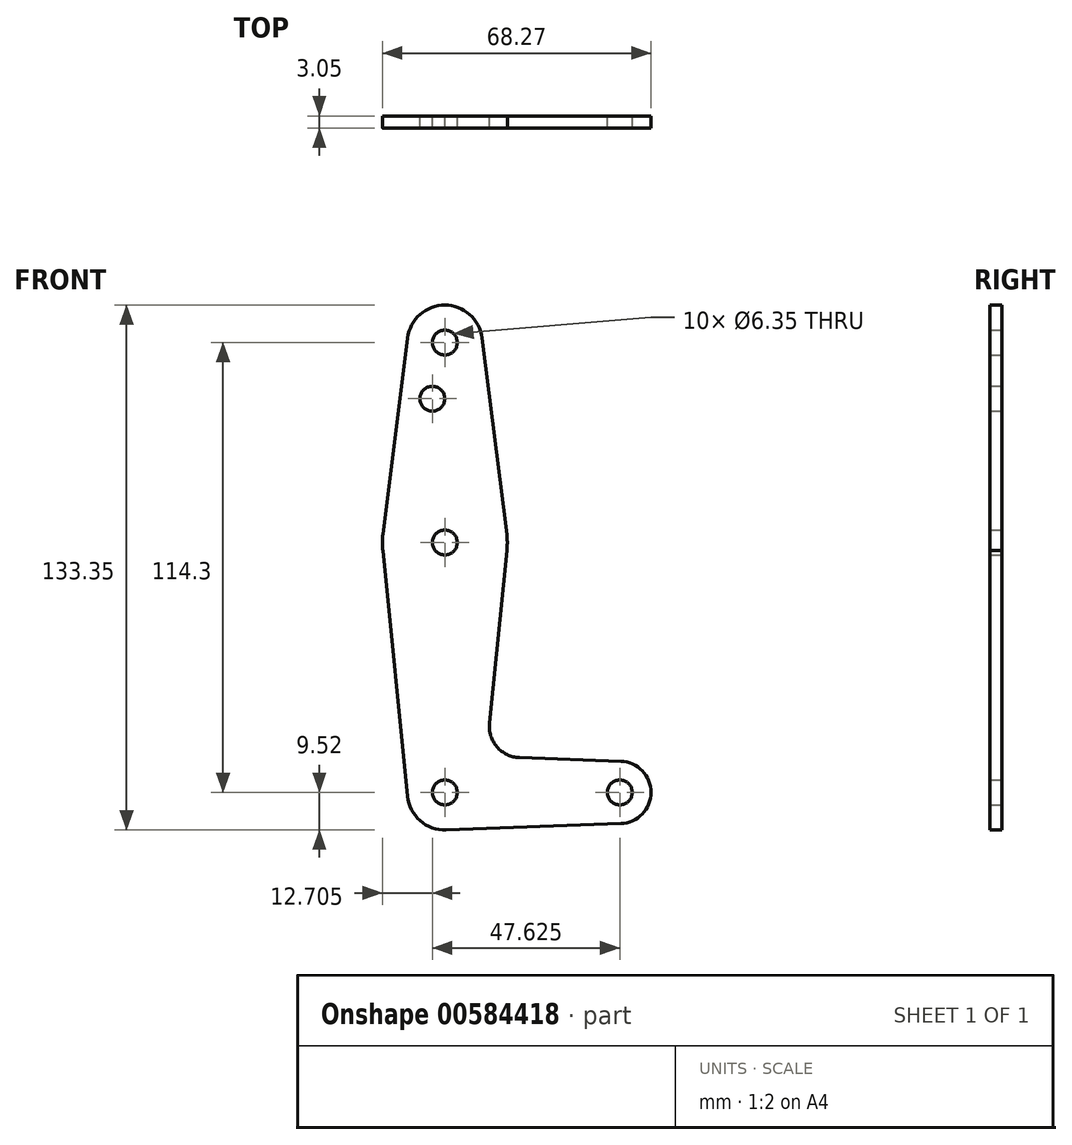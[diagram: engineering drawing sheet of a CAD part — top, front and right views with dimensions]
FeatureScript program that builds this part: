
annotation { "Feature Type Name" : "Feature", "Feature Type Description" : "" }
export const myFeature = defineFeature(function(context is Context, id is Id, definition is map)
    precondition{}
    {
        {
            var Q0;
            Q0=qCreatedBy(makeId("Front.planeOp"),FACE);
            var sketch = newSketch(context, id + "F0", { "sketchPlane" : qUnion([Q0])});
            skLineSegment(sketch, "E0", {"start": v(0, 0) * mm, "end": v(0, 63.5) * mm, "construction": true});
            skLineSegment(sketch, "E1", {"start": v(0, 63.5) * mm, "end": v(0, 114.3) * mm, "construction": true});
            skLineSegment(sketch, "E2", {"start": v(0, 0) * mm, "end": v(44.45, 0) * mm, "construction": true});
            skCircle(sketch, "E3", {"center": v(0, 0) * mm, "radius": 9.53 * mm});
            skCircle(sketch, "E4", {"center": v(44.45, 0) * mm, "radius": 7.94 * mm});
            skCircle(sketch, "E5", {"center": v(0, 63.5) * mm, "radius": 15.88 * mm});
            skCircle(sketch, "E6", {"center": v(0, 114.3) * mm, "radius": 9.53 * mm});
            skLineSegment(sketch, "E7", {"start": v(9.45, 115.5) * mm, "end": v(15.75, 65.48) * mm});
            skLineSegment(sketch, "E8", {"start": v(15.75, 61.52) * mm, "end": v(11.34, 17.6) * mm});
            skLineSegment(sketch, "E9", {"start": v(-9.45, 115.5) * mm, "end": v(-15.75, 65.48) * mm});
            skLineSegment(sketch, "E10", {"start": v(-15.75, 61.52) * mm, "end": v(-9.48, -0.95) * mm});
            skLineSegment(sketch, "E11", {"start": v(0.34, -9.52) * mm, "end": v(44.73, -7.93) * mm});
            skLineSegment(sketch, "E12", {"start": v(44.73, 7.93) * mm, "end": v(18.97, 8.85) * mm});
            skCircle(sketch, "E13", {"center": v(0, 114.3) * mm, "radius": 3.18 * mm});
            skCircle(sketch, "E14", {"center": v(0, 63.5) * mm, "radius": 3.18 * mm});
            skCircle(sketch, "E15", {"center": v(0, 0) * mm, "radius": 3.18 * mm});
            skCircle(sketch, "E16", {"center": v(44.45, 0) * mm, "radius": 3.18 * mm});
            skCircle(sketch, "E17", {"center": v(-3.17, 100.03) * mm, "radius": 3.18 * mm});
            skPoint(sketch, "E18.newPointB", {"position": v(0, 9.53) * mm});
            skArc(sketch, "E18.filletArc", {"start": v(11.34, 17.6) * mm, "mid": v(13.26, 11.57) * mm, "end": v(18.97, 8.85) * mm});
            skSolve(sketch);
        }
        {
            var Q0;
            Q0 = qSketchRegion(id + "F0", true);
            extrude(context, id + "F1", {"entities" : qUnion([Q0]), "depth" : 3.05 * mm, "offsetDistance" : 25.4 * mm});
        }
    });
